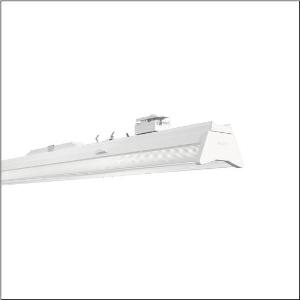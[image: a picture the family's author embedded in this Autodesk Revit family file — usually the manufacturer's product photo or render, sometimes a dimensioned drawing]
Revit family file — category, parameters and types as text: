
# Revit family: licross_11_performance_mo_51tm16cn49xg
name_source: partatom
category: Lighting Fixtures
units: mm (PartAtom-declared; Revit-internal decimal feet)

## family parameters
Cut with Voids When Loaded = No
Host = Face
Light Source = No
Part Type = Normal
Room Calculation Point = No
Round Connector Dimension = Use Diameter
Shared = No

## types (1)
- --- (1 x LED, 9190 lm, 49.4 W, 4000K)
    Apparent Load = 49 VA
    CIE Flux Codes = 66 88 96 79 100
    Color Rendering = 80
    Color Temperature = 4000K
    Default Elevation = 1800 mm
    Description = Licross 11 Performance MO, luminaire insert, of sheet steel, galvanised, coil coated, white, length: 1.500mm, width: 120mm, height: 123mm, LED rated luminous flux: 9.190lm, light colour: 840, SDCM (Standard Deviation of Colour Matching)MacAdam ≤ 2 SDCM (initial), control gear: ON/OFF Multilumen, CLOi, with plug, 3-pole, with phase selection, mains connection: 220..240V, AC, 50/60Hz, start of lifetime: 49W, end of service life: 55W, internal wiring halogen-free, primary light control with lens, of plastic, primary optical cover: cover, of PMMA, light emission: direct/indirect distribution, primary light characteristic: symmetric, protection rating (complete): IP40, insulation class (complete): insulation class I (protective earthing), certification: CE, ENEC, VDE, UKCA, protection symbol: D if used in an environment without relevant dust loads with corresponding accessories, impact resistance: IK06, permissible ambient temperature for indoor applications: -35..+40°C, corresponds to IFS (International Featured Standards) requirements for safety and quality in the food industry, reducing of maximum allowable ambient temperature of 5°C with ceiling mounting, LABS conformity tested according to VDMA 24364:2018-05, The light source and the operating device comply with the requirements of the Ecodesign Regulation (EU) 2019/2020 and are replaceable in accordance with this regulation, packaging unit: 1 piece
    Height = 114 mm
    Lamp = 1 x LED
    Lamp Light Flux = 9190 lm
    Lamp Power = 49.4 W
    Lamp count = 1
    Length = 1500 mm
    Luminous efficacy = 186 lm/W
    Manufacturer = Siteco
    ModVariant = No
    Model = 51TM16CN49XG
    Mounting Place = Ceiling
    Mounting Type = Pendant
    Number of Poles = 1
    OnlyDefault = Yes
    Power Factor = 1
    Product Name = Licross 11 Performance MO
    Product group = luminaire insert | ceiling pendant
    ProductGroupID = 901
    Protection Class = Protection class I
    Protection Degree = IP 40
    RLX_Detail_Level = 1
    RLX_Emergency_Light_Flux = 0 lm
    RLX_Emergency_Type = 0
    RLX_Emergency_Type_DB = No
    RlxData = <blob elided: 32089 chars, md5=650a8dd9>
    Socket = socket
    Standby Power = 0 W
    System Light Flux = 9190 lm
    System Power = 49 W
    Type Comments = factory setting: luminous flux: 100 % | (A | C | E) | 113 mA
    Type Image = l_1256138.jpg
    URL = http://relux.com
    VarID = @adj_001031
    Voltage = 0 V
    Weight = 0.00 kg
    Width = 120 mm

## geometry (parser evidence)
native form markers: Blend x4, Sweep x11
no freeform markers — native parametric forms only
